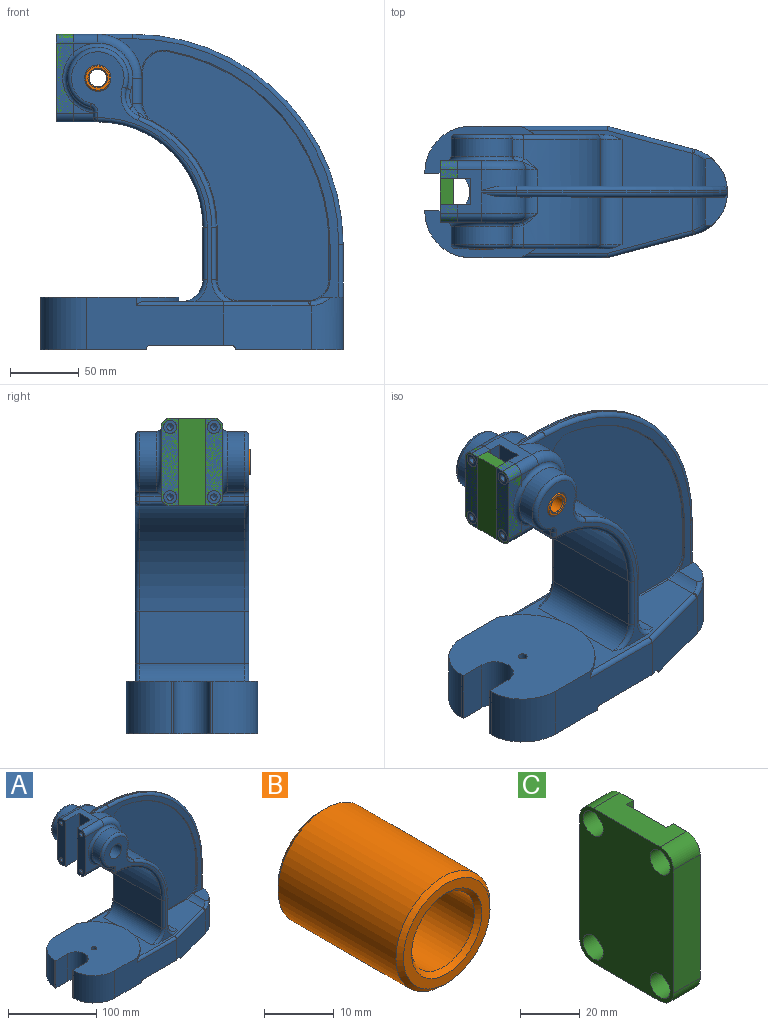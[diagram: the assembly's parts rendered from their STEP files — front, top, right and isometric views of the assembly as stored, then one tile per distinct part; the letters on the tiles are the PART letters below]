
ASSEMBLY  parts=3 mates=1
PART A: 180 faces, bbox 234.5x98.1x244 mm
  f0: plane 63.5x12.7mm, normal (-1,0,0), area 753.5mm2, adj f2,f15,f17,f92,f97,f149,f151,f158
  f1: plane 20.23x2.34mm, normal (0,1,0), area 23.9mm2, adj f90,f91,f104,f106
  f2: plane 50.8x30.1mm, normal (0,-1,0), area 515.4mm2, adj f0,f83,f92,f97,f124
  f3: plane 22.59x12.73mm, normal (1,0,0), area 235.4mm2, adj f19,f26,f32,f87,f94,f174
  f4: plane 22.59x12.73mm, normal (1,0,0), area 235.4mm2, adj f10,f14,f33,f86,f90,f164
  f5: plane 99.19x38.1mm, normal (0,-1,0), area 3202mm2, adj f6,f40,f46,f49,f52,f58,f76,f133
  f6: plane 100x95.25mm, normal (0,0,1), area 7398mm2, adj f5,f43,f44,f48,f54,f55,f56,f57
  f7: plane 38.1x34.96mm, normal (1,0,0), area 1331.9mm2, adj f8,f9,f114,f169
  f8: cylinder r=15.88mm len=34.96mm, axis (0,1,0), area 871.7mm2, adj f7,f37,f115,f167
  f9: cylinder r=85.72mm len=80.21mm, axis (0,1,0), area 3442.3mm2, adj f7,f80,f86,f100,f113,f168
  f10: cylinder r=15.88mm len=18.65mm, axis (0,1,0), area 22.7mm2, adj f4,f11,f33,f162
  f11: cylinder r=142.88mm len=140.67mm, axis (0,1,0), area 163.3mm2, adj f10,f12,f33,f160
  f12: plane 25.4x0.82mm, normal (-1,0,0), area 20.8mm2, adj f11,f13,f33,f161
  f13: cylinder r=15.88mm len=24.81mm, axis (0,1,0), area 242.1mm2, adj f12,f33,f37,f45,f139,f140,f163
  f14: cylinder r=31.75mm len=31.75mm, axis (0,1,0), area 616.8mm2, adj f4,f15,f33,f89,f141
  f15: plane 55.5x31.75mm, normal (0,0,1), area 573.2mm2, adj f0,f14,f16,f19,f31,f88,f92,f141
  f16: plane 63.5x12.7mm, normal (-1,0,0), area 753.5mm2, adj f15,f17,f21,f88,f96,f147,f153,f157
  f17: plane 31.75x30.1mm, normal (0,0,-1), area 533.2mm2, adj f0,f16,f18,f96,f97,f156,f157,f158
  f18: cylinder r=76.2mm len=76.2mm, axis (0,1,0), area 9120.7mm2, adj f17,f22,f103,f105,f119,f121
  f19: cylinder r=31.75mm len=31.75mm, axis (0,1,0), area 616.8mm2, adj f3,f15,f32,f93,f144
  f20: plane 20.23x2.34mm, normal (0,-1,0), area 23.9mm2, adj f94,f95,f122,f124
  f21: plane 50.8x30.1mm, normal (0,1,0), area 515.4mm2, adj f16,f78,f88,f96,f106
  f22: plane 76.2x38.1mm, normal (-1,0,0), area 2903.2mm2, adj f18,f98,f101,f117
  f23: cylinder r=15.88mm len=34.96mm, axis (0,1,0), area 871.7mm2, adj f24,f37,f132,f177
  f24: plane 38.1x34.96mm, normal (1,0,0), area 1331.9mm2, adj f23,f25,f131,f179
  f25: cylinder r=85.72mm len=80.21mm, axis (0,1,0), area 3442.3mm2, adj f24,f81,f87,f118,f130,f178
  f26: cylinder r=15.88mm len=18.65mm, axis (0,1,0), area 22.7mm2, adj f3,f27,f32,f172
  f27: cylinder r=142.88mm len=140.67mm, axis (0,1,0), area 163.3mm2, adj f26,f28,f32,f170
  f28: plane 25.4x0.82mm, normal (-1,0,0), area 20.8mm2, adj f27,f29,f32,f171
  f29: cylinder r=15.88mm len=24.81mm, axis (0,1,0), area 242.1mm2, adj f28,f32,f36,f37,f135,f136,f173
  f30: plane 76.2x7.92mm, normal (1,0,0), area 361.9mm2, adj f31,f36,f42,f45,f51,f53,f143,f146
  f31: cylinder r=152.4mm len=152.4mm, axis (0,1,0), area 377mm2, adj f15,f30,f142,f145
  f32: plane 187.33x160.79mm, normal (0,-1,0), area 1900.4mm2, adj f3,f19,f26,f27,f28,f29,f36,f144
  f33: plane 187.33x160.79mm, normal (0,1,0), area 1900.4mm2, adj f4,f10,f11,f12,f13,f14,f45,f141
  f34: plane 180.67x135mm, normal (0,-1,0), area 14138.8mm2, adj f170,f171,f172,f173,f174,f175,f176,f177
  f35: plane 180.67x135mm, normal (0,1,0), area 14138.8mm2, adj f160,f161,f162,f163,f164,f165,f166,f167
  f36: plane 26.58x18.73mm, normal (0,0,1), area 245.8mm2, adj f29,f30,f32,f53,f136,f146
  f37: plane 119.12x89.67mm, normal (0,0,1), area 4280.2mm2, adj f8,f13,f23,f29,f76,f77,f84,f98
  f38: cylinder r=3.17mm len=9.06mm, axis (0,1,0), area 40.9mm2, adj f40,f42,f52,f69
  f39: cylinder r=3.17mm len=7.93mm, axis (0,1,0), area 39.5mm2, adj f41,f46,f48,f65
  f40: plane 58.73x9.7mm, normal (0,0,-1), area 467.1mm2, adj f5,f38,f49,f52,f64,f69
  f41: plane 58.73x9.7mm, normal (0,0,-1), area 467.1mm2, adj f39,f47,f48,f50,f65,f67
  f42: plane 90.55x77.8mm, normal (0,0,-1), area 1454mm2, adj f30,f38,f47,f50,f51,f52,f53,f59
  f43: plane 38.1x1.61mm, normal (-1,0,0), area 61.5mm2, adj f6,f46,f54,f58
  f44: plane 38.1x1.61mm, normal (-1,0,0), area 61.5mm2, adj f6,f46,f55,f57
  f45: plane 26.58x18.73mm, normal (0,0,1), area 245.8mm2, adj f13,f30,f33,f51,f140,f143
  f46: plane 95.25x76.2mm, normal (0,0,-1), area 2029.8mm2, adj f5,f39,f43,f44,f48,f49,f54,f55
  f47: cylinder r=3.17mm len=9.06mm, axis (0,1,0), area 40.9mm2, adj f41,f42,f50,f67
  f48: plane 99.19x38.1mm, normal (0,1,0), area 3202mm2, adj f6,f39,f41,f46,f50,f57,f76,f137
  f49: cylinder r=3.17mm len=7.93mm, axis (0,1,0), area 39.5mm2, adj f5,f40,f46,f64
  f50: plane 63.64x32.15mm, normal (0.26,0.97,0), area 2053.6mm2, adj f41,f42,f47,f48,f51,f138,f139
  f51: cylinder r=31.75mm len=38.1mm, axis (0,0,-1), area 1379.2mm2, adj f30,f42,f45,f50,f140
  f52: plane 63.64x32.15mm, normal (0.26,-0.97,0), area 2053.6mm2, adj f5,f38,f40,f42,f53,f134,f135
  f53: cylinder r=31.75mm len=38.1mm, axis (0,0,-1), area 1379.2mm2, adj f30,f36,f42,f52,f136
  f54: plane 38.1x19.05mm, normal (0,1,0), area 725.8mm2, adj f6,f43,f46,f56
  f55: plane 38.1x19.05mm, normal (0,-1,0), area 725.8mm2, adj f6,f44,f46,f56
  f56: cylinder r=13.49mm len=38.1mm, axis (0,0,-1), area 1615.1mm2, adj f6,f46,f54,f55
  f57: cylinder r=33.32mm len=38.1mm, axis (0,0,-1), area 1963.7mm2, adj f6,f44,f46,f48
  f58: cylinder r=33.32mm len=38.1mm, axis (0,0,-1), area 1963.7mm2, adj f5,f6,f43,f46
  f59: plane 30.18x6.86mm, normal (-1,0,0), area 207mm2, adj f42,f60,f68,f70
  f60: plane 31.27x5.6mm, normal (0,0,-1), area 124.1mm2, adj f59,f61,f68,f70
  f61: cylinder r=23.8mm len=46.06mm, axis (0,1,0), area 499.2mm2, adj f60,f62,f67,f68,f69,f70
  f62: plane 84.13x79.4mm, normal (0,0,-1), area 5642.5mm2, adj f61,f64,f65,f66,f67,f69
  f63: plane 100.62x79.4mm, normal (0,0,-1), area 6568.5mm2, adj f64,f65,f66,f71,f72,f73,f74,f75
  f64: plane 98.15x30.18mm, normal (0,1,0), area 2718.8mm2, adj f40,f46,f49,f62,f63,f66,f69,f75
  f65: plane 98.15x30.18mm, normal (0,-1,0), area 2718.8mm2, adj f39,f41,f46,f62,f63,f66,f67,f74
  f66: plane 79.4x3.18mm, normal (-1,0,0), area 252.1mm2, adj f62,f63,f64,f65
  f67: plane 62.63x27.36mm, normal (-0.26,-0.97,0), area 1710.8mm2, adj f41,f42,f47,f61,f62,f65,f68
  f68: cylinder r=23.83mm len=30.18mm, axis (0,0,-1), area 814.8mm2, adj f42,f59,f60,f61,f67
  f69: plane 62.63x27.36mm, normal (-0.26,0.97,0), area 1710.8mm2, adj f38,f40,f42,f61,f62,f64,f70
  f70: cylinder r=23.83mm len=30.18mm, axis (0,0,-1), area 814.8mm2, adj f42,f59,f60,f61,f69
  f71: plane 30.18x10.12mm, normal (0,-1,0), area 305.3mm2, adj f46,f63,f73,f75
  f72: plane 30.18x10.12mm, normal (0,1,0), area 305.3mm2, adj f46,f63,f73,f74
  f73: cylinder r=21.42mm len=42.84mm, axis (0,0,-1), area 2030.4mm2, adj f46,f63,f71,f72
  f74: cylinder r=25.4mm len=30.18mm, axis (0,0,-1), area 986.2mm2, adj f46,f63,f65,f72
  f75: cylinder r=25.4mm len=30.18mm, axis (0,0,-1), area 986.2mm2, adj f46,f63,f64,f71
  f76: cylinder r=52.37mm len=95.25mm, axis (0,0,1), area 401mm2, adj f5,f6,f37,f48,f133,f137
  f77: plane 180.98x110.12mm, normal (0,1,0), area 1717.8mm2, adj f37,f85,f99,f101,f103,f109,f110,f111
  f78: plane 16.73x3.98mm, normal (-1,0,0), area 64.1mm2, adj f21,f96,f105,f106,f108,f109
  f79: cylinder r=22.23mm len=44.45mm, axis (0,1,0), area 1356.2mm2, adj f80,f106,f108,f111
  f80: cylinder r=15.88mm len=20.22mm, axis (0,1,0), area 319.4mm2, adj f9,f79,f102,f104,f112
  f81: cylinder r=15.88mm len=20.22mm, axis (0,1,0), area 319.4mm2, adj f25,f82,f120,f122,f129
  f82: cylinder r=22.23mm len=44.45mm, axis (0,1,0), area 1356.2mm2, adj f81,f124,f126,f128
  f83: plane 16.73x3.98mm, normal (-1,0,0), area 64.1mm2, adj f2,f97,f121,f124,f125,f126
  f84: plane 180.98x110.12mm, normal (0,-1,0), area 1717.8mm2, adj f37,f85,f116,f117,f119,f125,f127,f128
  f85: cylinder r=9.53mm len=82.55mm, axis (0,1,0), area 4727mm2, adj f77,f84,f156,f157,f158,f159
  f86: cylinder r=15.88mm len=14.02mm, axis (0,1,0), area 218.9mm2, adj f4,f9,f91,f166
  f87: cylinder r=15.88mm len=14.02mm, axis (0,1,0), area 218.9mm2, adj f3,f25,f95,f176
  f88: cylinder r=6.35mm len=30.1mm, axis (-1,0,0), area 300.2mm2, adj f15,f16,f21,f89
  f89: torus R=25.4mm, axis (0,-1,0), area 461.3mm2, adj f14,f88,f90,f106
  f90: cylinder r=6.35mm len=18.2mm, axis (0,0,1), area 181.6mm2, adj f1,f4,f89,f91
  f91: torus R=22.23mm, axis (0,-1,0), area 98mm2, adj f1,f86,f90,f100,f102
  f92: cylinder r=6.35mm len=30.1mm, axis (1,0,0), area 300.2mm2, adj f0,f2,f15,f93
  f93: torus R=25.4mm, axis (0,-1,0), area 461.3mm2, adj f19,f92,f94,f124
  f94: cylinder r=6.35mm len=18.2mm, axis (0,0,-1), area 181.6mm2, adj f3,f20,f93,f95
  f95: torus R=22.23mm, axis (0,-1,0), area 98mm2, adj f20,f87,f94,f118,f120
  f96: cylinder r=6.35mm len=30.1mm, axis (1,0,0), area 279.1mm2, adj f16,f17,f21,f78,f105
  f97: cylinder r=6.35mm len=30.1mm, axis (-1,0,0), area 279.1mm2, adj f0,f2,f17,f83,f121
  f98: cylinder r=15.88mm len=76.2mm, axis (0,-1,0), area 1900.2mm2, adj f22,f37,f99,f116
  f99: torus R=19.05mm, axis (0,-1,0), area 107.7mm2, adj f37,f77,f98,f101
  f100: bspline ~12.01x8.85mm, area 17.9mm2, adj f9,f91,f102
  f101: cylinder r=3.17mm len=38.1mm, axis (0,0,-1), area 190mm2, adj f22,f77,f99,f103
  f102: bspline ~10.6x9.56mm, area 36.6mm2, adj f80,f91,f100,f104
  f103: torus R=79.38mm, axis (0,-1,0), area 606mm2, adj f18,f77,f101,f107
  f104: torus R=12.7mm, axis (0,-1,0), area 70.6mm2, adj f1,f80,f102,f106
  f105: cylinder r=3.17mm len=22.23mm, axis (0,1,0), area 97.1mm2, adj f18,f78,f96,f107
  f106: torus R=25.4mm, axis (0,-1,0), area 570mm2, adj f1,f21,f78,f79,f89,f104,f108
  f107: sphere r=3.17mm, area 21.6mm2, adj f103,f105,f109
  f108: cylinder r=3.17mm len=15.82mm, axis (0,1,0), area 59.7mm2, adj f78,f79,f106,f110
  f109: cylinder r=3.17mm len=3.98mm, axis (0,0,-1), area 19.9mm2, adj f77,f78,f107,f110
  f110: torus R=6.35mm, axis (0,-1,0), area 28.5mm2, adj f77,f108,f109,f111
  f111: torus R=19.05mm, axis (0,-1,0), area 504.9mm2, adj f77,f79,f110,f112
  f112: torus R=19.05mm, axis (0,-1,0), area 132.1mm2, adj f77,f80,f111,f113
  f113: torus R=82.55mm, axis (0,-1,0), area 510.4mm2, adj f9,f77,f112,f114
  f114: cylinder r=3.17mm len=38.1mm, axis (0,0,1), area 190mm2, adj f7,f77,f113,f115
  f115: torus R=19.05mm, axis (0,-1,0), area 107.7mm2, adj f8,f37,f77,f114
  f116: torus R=19.05mm, axis (0,-1,0), area 107.7mm2, adj f37,f84,f98,f117
  f117: cylinder r=3.17mm len=38.1mm, axis (0,0,1), area 190mm2, adj f22,f84,f116,f119
  f118: bspline ~11.06x8.44mm, area 17.9mm2, adj f25,f95,f120
  f119: torus R=79.38mm, axis (0,-1,0), area 606mm2, adj f18,f84,f117,f123
  f120: bspline ~9.12x8.99mm, area 36.6mm2, adj f81,f95,f118,f122
  f121: cylinder r=3.17mm len=22.23mm, axis (0,1,0), area 97.1mm2, adj f18,f83,f97,f123
  f122: torus R=12.7mm, axis (0,-1,0), area 70.6mm2, adj f20,f81,f120,f124
  f123: sphere r=3.17mm, area 15.8mm2, adj f119,f121,f125
  f124: torus R=25.4mm, axis (0,-1,0), area 570mm2, adj f2,f20,f82,f83,f93,f122,f126
  f125: cylinder r=3.17mm len=3.98mm, axis (0,0,1), area 19.9mm2, adj f83,f84,f123,f127
  f126: cylinder r=3.17mm len=15.82mm, axis (0,1,0), area 59.7mm2, adj f82,f83,f124,f127
  f127: torus R=6.35mm, axis (0,-1,0), area 28.5mm2, adj f84,f125,f126,f128
  f128: torus R=19.05mm, axis (0,-1,0), area 504.9mm2, adj f82,f84,f127,f129
  f129: torus R=19.05mm, axis (0,-1,0), area 132.1mm2, adj f81,f84,f128,f130
  f130: torus R=82.55mm, axis (0,-1,0), area 510.4mm2, adj f25,f84,f129,f131
  f131: cylinder r=3.17mm len=38.1mm, axis (0,0,-1), area 190mm2, adj f24,f84,f130,f132
  f132: torus R=19.05mm, axis (0,-1,0), area 107.7mm2, adj f23,f37,f84,f131
  f133: cylinder r=3.17mm len=63.09mm, axis (1,0,0), area 298.9mm2, adj f5,f37,f76,f134
  f134: cylinder r=3.17mm len=62.81mm, axis (0.97,0.26,0), area 319mm2, adj f37,f52,f133,f135
  f135: bspline ~3.41x3.21mm, area 6mm2, adj f29,f52,f134,f136
  f136: bspline ~18.95x11.92mm, area 79.7mm2, adj f29,f36,f53,f135
  f137: cylinder r=3.17mm len=63.09mm, axis (-1,0,0), area 298.9mm2, adj f37,f48,f76,f138
  f138: cylinder r=3.17mm len=62.81mm, axis (-0.97,0.26,0), area 319mm2, adj f37,f50,f137,f139
  f139: bspline ~6.89x4.84mm, area 6mm2, adj f13,f50,f138,f140
  f140: bspline ~17.46x11.57mm, area 79.7mm2, adj f13,f45,f51,f139
  f141: cylinder r=3.17mm len=25.4mm, axis (-1,0,0), area 92.2mm2, adj f14,f15,f33,f142
  f142: torus R=149.22mm, axis (0,-1,0), area 1184.9mm2, adj f31,f33,f141,f143
  f143: cylinder r=3.17mm len=38.1mm, axis (0,0,1), area 190mm2, adj f30,f33,f45,f142
  f144: cylinder r=3.17mm len=25.4mm, axis (1,0,0), area 92.2mm2, adj f15,f19,f32,f145
  f145: torus R=149.22mm, axis (0,-1,0), area 1184.9mm2, adj f31,f32,f144,f146
  f146: cylinder r=3.17mm len=38.1mm, axis (0,0,-1), area 190mm2, adj f30,f32,f36,f145
  f147: cylinder r=2.38mm len=6.35mm, axis (-1,0,0), area 95mm2, adj f16,f148
  f148: cone r=0mm half-angle=59deg, axis (-1,0,0), area 20.8mm2, adj f147
  f149: cylinder r=2.38mm len=6.35mm, axis (-1,0,0), area 95mm2, adj f0,f150
  f150: cone r=0mm half-angle=59deg, axis (-1,0,0), area 20.8mm2, adj f149
  f151: cylinder r=2.38mm len=6.35mm, axis (-1,0,0), area 95mm2, adj f0,f152
  f152: cone r=0mm half-angle=59deg, axis (-1,0,0), area 20.8mm2, adj f151
  f153: cylinder r=2.38mm len=6.35mm, axis (-1,0,0), area 95mm2, adj f16,f154
  f154: cone r=0mm half-angle=59deg, axis (-1,0,0), area 20.8mm2, adj f153
  f155: cylinder r=3.17mm len=7.93mm, axis (0,0,1), area 158.1mm2, adj f6,f63
  f156: plane 26.47x19.05mm, normal (-1,0,0), area 504.2mm2, adj f17,f85,f157,f158
  f157: plane 63.5x22.17mm, normal (0,-1,0), area 1396.6mm2, adj f15,f16,f17,f85,f156,f159
  f158: plane 63.5x22.17mm, normal (0,1,0), area 1396.6mm2, adj f0,f15,f17,f85,f156,f159
  f159: plane 26.47x19.05mm, normal (-1,0,0), area 504.2mm2, adj f15,f85,f157,f158
  f160: torus R=142.11mm, axis (0,-1,0), area 238.1mm2, adj f11,f35,f161,f162
  f161: cylinder r=0.76mm len=25.4mm, axis (0,0,1), area 30.4mm2, adj f12,f35,f160,f163
  f162: torus R=15.11mm, axis (0,-1,0), area 32.6mm2, adj f10,f35,f160,f164
  f163: torus R=15.11mm, axis (0,-1,0), area 29.3mm2, adj f13,f35,f161,f165
  f164: cylinder r=0.76mm len=22.59mm, axis (0,0,1), area 27mm2, adj f4,f35,f162,f166
  f165: cylinder r=0.76mm len=50.8mm, axis (1,0,0), area 60.8mm2, adj f35,f37,f163,f167
  f166: torus R=15.11mm, axis (0,-1,0), area 20.2mm2, adj f35,f86,f164,f168
  f167: torus R=15.11mm, axis (0,-1,0), area 29.3mm2, adj f8,f35,f165,f169
  f168: torus R=86.49mm, axis (0,-1,0), area 111.5mm2, adj f9,f35,f166,f169
  f169: cylinder r=0.76mm len=38.1mm, axis (0,0,-1), area 45.6mm2, adj f7,f35,f167,f168
  f170: torus R=142.11mm, axis (0,-1,0), area 238.1mm2, adj f27,f34,f171,f172
  f171: cylinder r=0.76mm len=25.4mm, axis (0,0,-1), area 30.4mm2, adj f28,f34,f170,f173
  f172: torus R=15.11mm, axis (0,-1,0), area 32.6mm2, adj f26,f34,f170,f174
  f173: torus R=15.11mm, axis (0,-1,0), area 29.3mm2, adj f29,f34,f171,f175
  f174: cylinder r=0.76mm len=22.59mm, axis (0,0,-1), area 27mm2, adj f3,f34,f172,f176
  f175: cylinder r=0.76mm len=50.8mm, axis (-1,0,0), area 60.8mm2, adj f34,f37,f173,f177
  f176: torus R=15.11mm, axis (0,-1,0), area 20.2mm2, adj f34,f87,f174,f178
  f177: torus R=15.11mm, axis (0,-1,0), area 29.3mm2, adj f23,f34,f175,f179
  f178: torus R=86.49mm, axis (0,-1,0), area 111.5mm2, adj f25,f34,f176,f179
  f179: cylinder r=0.76mm len=38.1mm, axis (0,0,1), area 45.6mm2, adj f24,f34,f177,f178
PART B: 8 faces, bbox 19.1x25.4x19.1 mm
  f0: plane 17.53x17.53mm, normal (0,-1,0), area 82.3mm2, adj f4,f5
  f1: plane 17.53x17.53mm, normal (0,1,0), area 82.3mm2, adj f6,f7
  f2: cylinder r=9.53mm len=23.88mm, axis (0,1,0), area 1428.9mm2, adj f4,f7
  f3: cylinder r=6.35mm len=23.88mm, axis (0,1,0), area 952.6mm2, adj f5,f6
  f4: cone r=9.53mm half-angle=45deg, axis (0,1,0), area 61.9mm2, adj f0,f2
  f5: cone r=6.35mm half-angle=45deg, axis (0,-1,0), area 45.6mm2, adj f0,f3
  f6: cone r=6.35mm half-angle=45deg, axis (0,1,0), area 45.6mm2, adj f1,f3
  f7: cone r=9.53mm half-angle=45deg, axis (0,-1,0), area 61.9mm2, adj f1,f2
PART C: 26 faces, bbox 12.7x44.5x63.5 mm
  f0: plane 63.5x12.7mm, normal (1,0,0), area 753.5mm2, adj f1,f2,f6,f7,f8,f14,f17,f25
  f1: cylinder r=6.35mm len=12.7mm, axis (1,0,0), area 126.7mm2, adj f0,f2,f8,f9
  f2: plane 31.75x12.7mm, normal (0,0,1), area 341.8mm2, adj f0,f1,f3,f9,f10,f23,f24,f25
  f3: cylinder r=6.35mm len=12.7mm, axis (1,0,0), area 126.7mm2, adj f2,f4,f9,f10
  f4: plane 50.8x12.7mm, normal (0,1,0), area 645.2mm2, adj f3,f5,f9,f10
  f5: cylinder r=6.35mm len=12.7mm, axis (1,0,0), area 126.7mm2, adj f4,f6,f9,f10
  f6: plane 31.75x12.7mm, normal (0,0,-1), area 341.8mm2, adj f0,f5,f7,f9,f10,f23,f24,f25
  f7: cylinder r=6.35mm len=12.7mm, axis (1,0,0), area 126.7mm2, adj f0,f6,f8,f9
  f8: plane 50.8x12.7mm, normal (0,-1,0), area 645.2mm2, adj f0,f1,f7,f9
  f9: plane 63.5x44.45mm, normal (-1,0,0), area 2502.9mm2, adj f1,f2,f3,f4,f5,f6,f7,f8
  f10: plane 63.5x12.7mm, normal (1,0,0), area 753.5mm2, adj f2,f3,f4,f5,f6,f11,f20,f24
  f11: cylinder r=2.38mm len=6.35mm, axis (-1,0,0), area 95mm2, adj f10,f12
  f12: plane 9.53x9.53mm, normal (-1,0,0), area 53.4mm2, adj f11,f13
  f13: cylinder r=4.76mm len=9.53mm, axis (-1,0,0), area 190mm2, adj f9,f12
  f14: cylinder r=2.38mm len=6.35mm, axis (-1,0,0), area 95mm2, adj f0,f15
  f15: plane 9.53x9.53mm, normal (-1,0,0), area 53.4mm2, adj f14,f16
  f16: cylinder r=4.76mm len=9.53mm, axis (-1,0,0), area 190mm2, adj f9,f15
  f17: cylinder r=2.38mm len=6.35mm, axis (-1,0,0), area 95mm2, adj f0,f18
  f18: plane 9.53x9.53mm, normal (-1,0,0), area 53.4mm2, adj f17,f19
  f19: cylinder r=4.76mm len=9.53mm, axis (-1,0,0), area 190mm2, adj f9,f18
  f20: cylinder r=2.38mm len=6.35mm, axis (-1,0,0), area 95mm2, adj f10,f21
  f21: plane 9.53x9.53mm, normal (-1,0,0), area 53.4mm2, adj f20,f22
  f22: cylinder r=4.76mm len=9.53mm, axis (-1,0,0), area 190mm2, adj f9,f21
  f23: plane 63.5x19.05mm, normal (1,0,0), area 1209.7mm2, adj f2,f6,f24,f25
  f24: plane 63.5x3.23mm, normal (0,-1,0), area 204.8mm2, adj f2,f6,f10,f23
  f25: plane 63.5x3.23mm, normal (0,1,0), area 204.8mm2, adj f0,f2,f6,f23
PLACE A t=(-21.17,43.65,7.67)mm
PLACE B t=(-21.17,-14.26,7.67)mm
PLACE C t=(-8.47,43.65,7.67)mm
MATE fastened B.f2 <-> A.f14  axis (0,1,0) through (-21.17,2.38,7.67)mm
